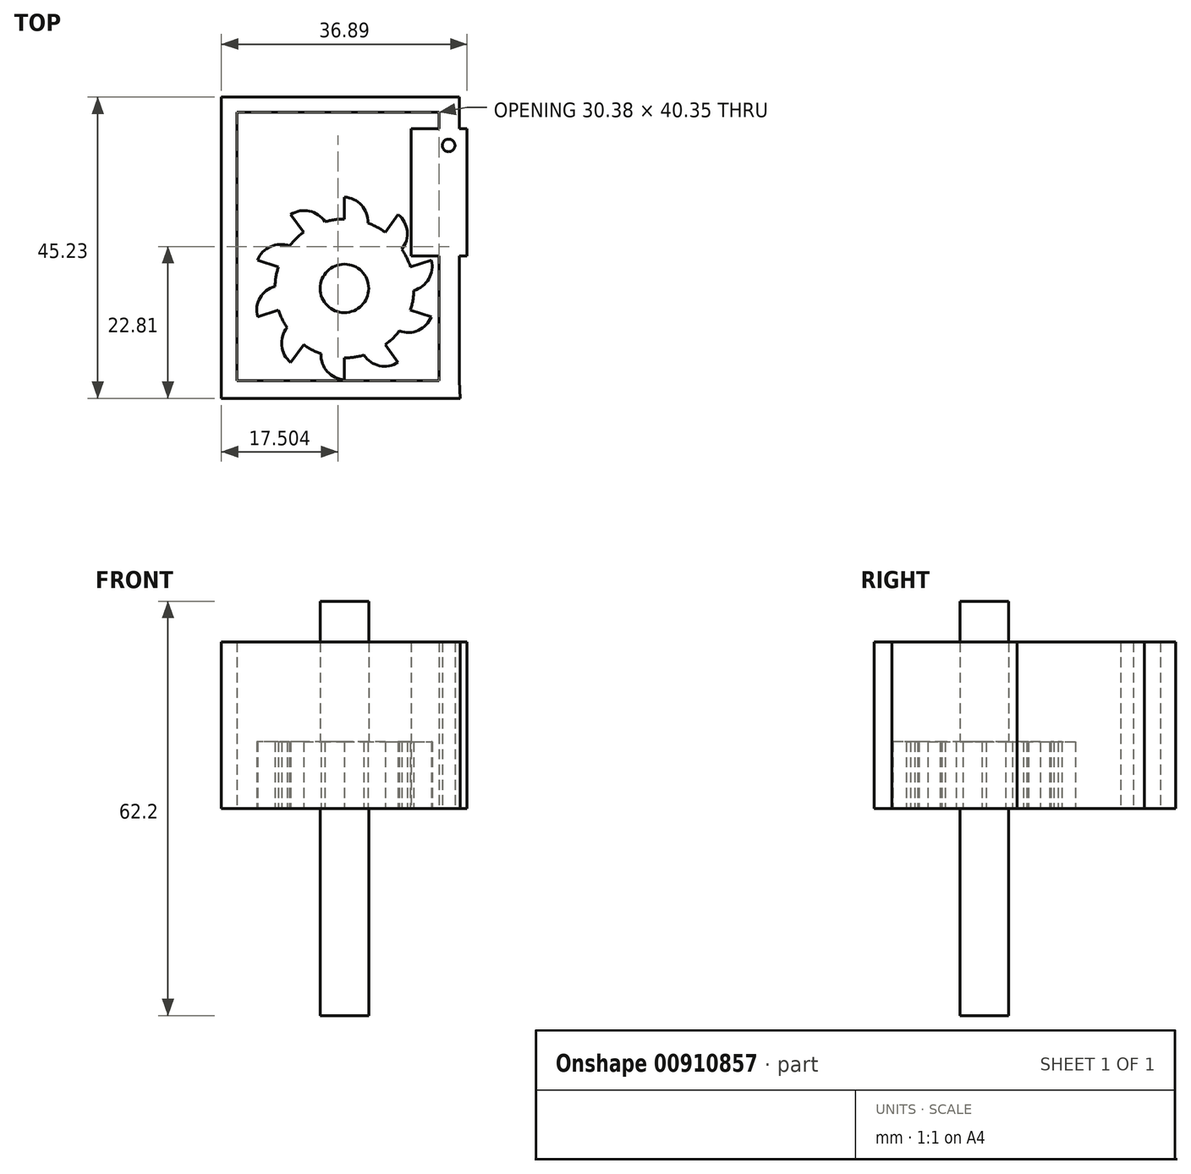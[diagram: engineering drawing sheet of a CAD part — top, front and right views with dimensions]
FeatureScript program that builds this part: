
annotation { "Feature Type Name" : "Feature", "Feature Type Description" : "" }
export const myFeature = defineFeature(function(context is Context, id is Id, definition is map)
    precondition{}
    {
        {
            var Q0;
            Q0=qCreatedBy(makeId("Top.planeOp"),FACE);
            var sketch = newSketch(context, id + "F0", { "sketchPlane" : qUnion([Q0])});
            skCircle(sketch, "E0", {"center": v(0, 0) * mm, "radius": 3.64 * mm});
            skArc(sketch, "E1", {"start": v(-6.13, 8.44) * mm, "mid": v(-7.27, 7.48) * mm, "end": v(-8.25, 6.38) * mm});
            skLineSegment(sketch, "E2", {"start": v(0, 10.43) * mm, "end": v(0, 13.72) * mm});
            skArc(sketch, "E3", {"start": v(3.51, 9.82) * mm, "mid": v(2.56, 12.5) * mm, "end": v(0, 13.72) * mm});
            skArc(sketch, "E4.1.0", {"start": v(-2.93, 10.01) * mm, "mid": v(-5.27, 11.61) * mm, "end": v(-8.06, 11.1) * mm});
            skLineSegment(sketch, "E4.1.1", {"start": v(-6.13, 8.44) * mm, "end": v(-8.06, 11.1) * mm});
            skArc(sketch, "E4.2.0", {"start": v(-8.25, 6.38) * mm, "mid": v(-11.1, 6.3) * mm, "end": v(-13.04, 4.24) * mm});
            skLineSegment(sketch, "E4.2.1", {"start": v(-9.92, 3.22) * mm, "end": v(-13.04, 4.24) * mm});
            skArc(sketch, "E4.3.0", {"start": v(-10.43, 0.3) * mm, "mid": v(-12.67, -1.42) * mm, "end": v(-13.04, -4.24) * mm});
            skLineSegment(sketch, "E4.3.1", {"start": v(-9.92, -3.22) * mm, "end": v(-13.04, -4.24) * mm});
            skArc(sketch, "E4.4.0", {"start": v(-8.62, -5.88) * mm, "mid": v(-9.42, -8.6) * mm, "end": v(-8.06, -11.1) * mm});
            skLineSegment(sketch, "E4.4.1", {"start": v(-6.13, -8.44) * mm, "end": v(-8.06, -11.1) * mm});
            skArc(sketch, "E4.5.0", {"start": v(-3.51, -9.82) * mm, "mid": v(-2.56, -12.5) * mm, "end": v(0, -13.72) * mm});
            skLineSegment(sketch, "E4.5.1", {"start": v(0, -10.43) * mm, "end": v(0, -13.72) * mm});
            skArc(sketch, "E4.6.0", {"start": v(2.93, -10.01) * mm, "mid": v(5.27, -11.61) * mm, "end": v(8.06, -11.1) * mm});
            skLineSegment(sketch, "E4.6.1", {"start": v(6.13, -8.44) * mm, "end": v(8.06, -11.1) * mm});
            skArc(sketch, "E4.7.0", {"start": v(8.25, -6.38) * mm, "mid": v(11.1, -6.3) * mm, "end": v(13.04, -4.24) * mm});
            skLineSegment(sketch, "E4.7.1", {"start": v(9.92, -3.22) * mm, "end": v(13.04, -4.24) * mm});
            skArc(sketch, "E4.8.0", {"start": v(10.43, -0.3) * mm, "mid": v(12.67, 1.42) * mm, "end": v(13.04, 4.24) * mm});
            skLineSegment(sketch, "E4.8.1", {"start": v(9.92, 3.22) * mm, "end": v(13.04, 4.24) * mm});
            skArc(sketch, "E4.9.0", {"start": v(8.62, 5.88) * mm, "mid": v(9.42, 8.6) * mm, "end": v(8.06, 11.1) * mm});
            skLineSegment(sketch, "E4.9.1", {"start": v(6.13, 8.44) * mm, "end": v(8.06, 11.1) * mm});
            skArc(sketch, "E5.trimOffspring", {"start": v(0, 10.43) * mm, "mid": v(-1.48, 10.32) * mm, "end": v(-2.93, 10.01) * mm});
            skArc(sketch, "E6.trimOffspring", {"start": v(6.13, 8.44) * mm, "mid": v(4.87, 9.22) * mm, "end": v(3.51, 9.82) * mm});
            skArc(sketch, "E7.trimOffspring", {"start": v(9.92, 3.22) * mm, "mid": v(9.36, 4.6) * mm, "end": v(8.62, 5.88) * mm});
            skArc(sketch, "E8.trimOffspring", {"start": v(9.92, -3.22) * mm, "mid": v(10.28, -1.78) * mm, "end": v(10.43, -0.3) * mm});
            skArc(sketch, "E9.trimOffspring", {"start": v(6.13, -8.44) * mm, "mid": v(7.27, -7.48) * mm, "end": v(8.25, -6.38) * mm});
            skArc(sketch, "E10.trimOffspring", {"start": v(0, -10.43) * mm, "mid": v(1.48, -10.32) * mm, "end": v(2.93, -10.01) * mm});
            skArc(sketch, "E11.trimOffspring", {"start": v(-6.13, -8.44) * mm, "mid": v(-4.87, -9.22) * mm, "end": v(-3.51, -9.82) * mm});
            skArc(sketch, "E12.trimOffspring", {"start": v(-9.92, -3.22) * mm, "mid": v(-9.36, -4.6) * mm, "end": v(-8.62, -5.88) * mm});
            skArc(sketch, "E13.trimOffspring", {"start": v(-9.92, 3.22) * mm, "mid": v(-10.28, 1.78) * mm, "end": v(-10.43, 0.3) * mm});
            skSolve(sketch);
        }
        {
            var Q0;
            Q0=makeQuery(id+"F0.imprint","IMPRINT",FACE,{"disambiguationData":[TD([[makeQuery(id+"F0.imprint","IMPRINT",EDGE,{"derivedFrom":sQuery(id+"F0.wireOp",EDGE,"E0")}),-1.0]])]});
            extrude(context, id + "F1", {"entities" : qUnion([Q0]), "depth" : 10 * mm, "offsetDistance" : 25 * mm});
        }
        {
            var Q0;
            Q0=qCreatedBy(makeId("Top.planeOp"),FACE);
            var sketch = newSketch(context, id + "F2", { "sketchPlane" : qUnion([Q0])});
            skLineSegment(sketch, "E14.bottom", {"start": v(10.02, 4.9) * mm, "end": v(18.41, 4.9) * mm});
            skLineSegment(sketch, "E14.top", {"start": v(10.02, 24.02) * mm, "end": v(18.41, 24.02) * mm});
            skLineSegment(sketch, "E14.left", {"start": v(10.02, 4.9) * mm, "end": v(10.02, 24.02) * mm});
            skLineSegment(sketch, "E14.right", {"start": v(18.41, 4.9) * mm, "end": v(18.41, 24.02) * mm});
            skPoint(sketch, "E15.firstSnap0", {"position": v(14.21, 24.02) * mm});
            skLineSegment(sketch, "E15.left", {"start": v(14.21, -13.88) * mm, "end": v(14.21, 4.9) * mm});
            skLineSegment(sketch, "E15.right", {"start": v(17.26, -13.88) * mm, "end": v(17.26, 4.9) * mm});
            skCircle(sketch, "E16", {"center": v(15.65, 21.47) * mm, "radius": 0.95 * mm});
            skLineSegment(sketch, "E17", {"start": v(14.21, -13.88) * mm, "end": v(-16.17, -13.88) * mm});
            skLineSegment(sketch, "E18", {"start": v(-16.17, -16.5) * mm, "end": v(17.39, -16.5) * mm});
            skLineSegment(sketch, "E19", {"start": v(17.39, -16.5) * mm, "end": v(17.26, -13.88) * mm});
            skLineSegment(sketch, "E20", {"start": v(14.21, 26.48) * mm, "end": v(-16.17, 26.48) * mm});
            skLineSegment(sketch, "E21", {"start": v(-16.17, 26.48) * mm, "end": v(-16.17, -13.88) * mm});
            skLineSegment(sketch, "E22", {"start": v(-16.17, -16.5) * mm, "end": v(-18.48, -16.5) * mm});
            skLineSegment(sketch, "E23", {"start": v(-18.48, -16.5) * mm, "end": v(-18.48, 28.72) * mm});
            skLineSegment(sketch, "E24", {"start": v(-18.48, 28.72) * mm, "end": v(17.26, 28.72) * mm});
            skLineSegment(sketch, "E25", {"start": v(17.26, 28.72) * mm, "end": v(17.26, 26.48) * mm});
            skLineSegment(sketch, "E26.trimOffspring", {"start": v(14.21, 24.02) * mm, "end": v(14.21, 26.48) * mm});
            skLineSegment(sketch, "E27.trimOffspring", {"start": v(17.26, 24.02) * mm, "end": v(17.26, 26.48) * mm});
            skSolve(sketch);
        }
        {
            var Q0;
            {var subQ0=sQuery(id+"F2.wireOp",EDGE,"E15.left");Q0=makeQuery(id+"F2.imprint","IMPRINT",FACE,{"disambiguationData":[TD([[makeQuery(id+"F2.imprint","IMPRINT",EDGE,{"derivedFrom":subQ0}),-1.0]])]});}
            var Q1;
            {var subQ0=sQuery(id+"F2.wireOp",EDGE,"E14.left");Q1=makeQuery(id+"F2.imprint","IMPRINT",FACE,{"disambiguationData":[TD([[makeQuery(id+"F2.imprint","IMPRINT",EDGE,{"derivedFrom":subQ0}),-1.0]])]});}
            extrude(context, id + "F3", {"entities" : qUnion([Q0, Q1]), "depth" : 25 * mm, "offsetDistance" : 25 * mm});
        }
        {
            var Q0;
            Q0=makeQuery(id+"F0.imprint","IMPRINT",FACE,{"disambiguationData":[TD([[makeQuery(id+"F0.imprint","IMPRINT",EDGE,{"derivedFrom":sQuery(id+"F0.wireOp",EDGE,"E0")}),1.0]])]});
            extrude(context, id + "F4", {"entities" : qUnion([Q0]), "operationType" : NewBodyOperationType.ADD, "endBound" : BoundingType.SYMMETRIC, "depth" : 62.2 * mm, "offsetDistance" : 25 * mm});
        }
    });
